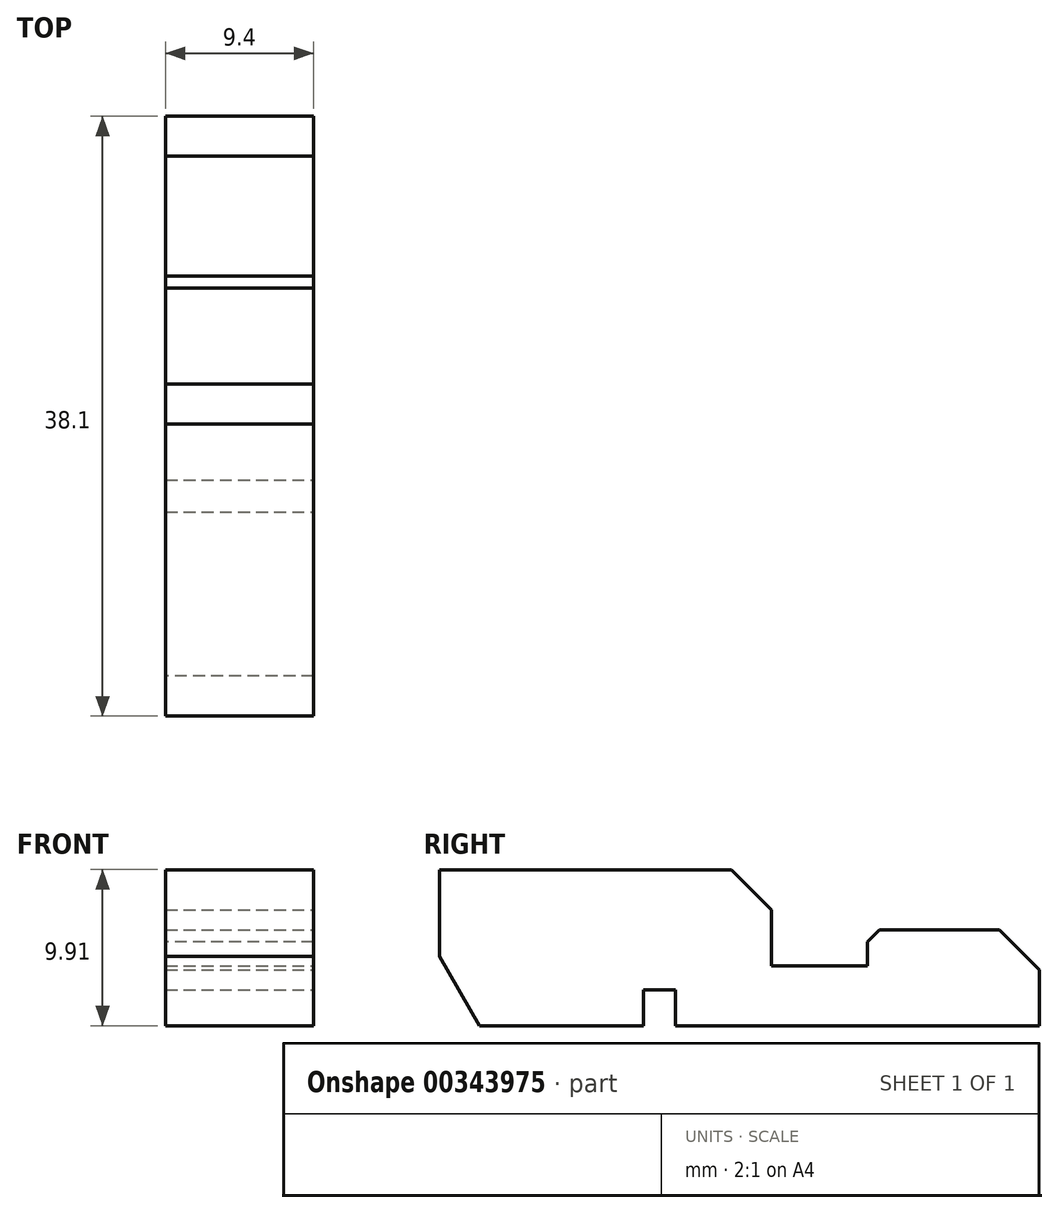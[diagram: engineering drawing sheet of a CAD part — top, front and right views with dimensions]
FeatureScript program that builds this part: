
annotation { "Feature Type Name" : "Feature", "Feature Type Description" : "" }
export const myFeature = defineFeature(function(context is Context, id is Id, definition is map)
    precondition{}
    {
        {
            var Q0;
            Q0=qCreatedBy(makeId("Top.planeOp"),FACE);
            var sketch = newSketch(context, id + "F0", { "sketchPlane" : qUnion([Q0])});
            skLineSegment(sketch, "E0.bottom", {"start": v(4.7, 19.05) * mm, "end": v(-4.7, 19.05) * mm});
            skLineSegment(sketch, "E0.top", {"start": v(4.7, -19.05) * mm, "end": v(-4.7, -19.05) * mm});
            skLineSegment(sketch, "E0.left", {"start": v(4.7, 19.05) * mm, "end": v(4.7, -19.05) * mm});
            skLineSegment(sketch, "E0.right", {"start": v(-4.7, 19.05) * mm, "end": v(-4.7, -19.05) * mm});
            skPoint(sketch, "E0.middle", {"position": v(0, 0) * mm});
            skSolve(sketch);
        }
        {
            var Q0;
            Q0=makeQuery(id+"F0.imprint","IMPRINT",FACE,{"disambiguationData":[TD([[makeQuery(id+"F0.imprint","IMPRINT",EDGE,{"derivedFrom":sQuery(id+"F0.wireOp",EDGE,"E0.bottom")}),1.0]])]});
            extrude(context, id + "F1", {"entities" : qUnion([Q0]), "depth" : 6.1 * mm});
        }
        {
            var Q0;
            Q0=makeQuery(id+"F1.opExtrude","CAP_FACE",FACE,{"disambiguationData":[OSD([sQuery(id+"F0.wireOp",EDGE,"E0.bottom"),sQuery(id+"F0.wireOp",EDGE,"E0.top"),sQuery(id+"F0.wireOp",EDGE,"E0.left"),sQuery(id+"F0.wireOp",EDGE,"E0.right")])],"isStart":false});
            var sketch = newSketch(context, id + "F2", { "sketchPlane" : qUnion([Q0])});
            skPoint(sketch, "E1", {"position": v(-4.7, 5.08) * mm});
            skPoint(sketch, "E2", {"position": v(4.7, 5.08) * mm});
            skPoint(sketch, "E3", {"position": v(0, 5.08) * mm});
            skLineSegment(sketch, "E4.bottom", {"start": v(-4.7, 8.13) * mm, "end": v(4.7, 8.13) * mm});
            skLineSegment(sketch, "E4.top", {"start": v(-4.7, 2.03) * mm, "end": v(4.7, 2.03) * mm});
            skLineSegment(sketch, "E4.left", {"start": v(-4.7, 8.13) * mm, "end": v(-4.7, 2.03) * mm});
            skLineSegment(sketch, "E4.right", {"start": v(4.7, 8.13) * mm, "end": v(4.7, 2.03) * mm});
            skLineSegment(sketch, "E5", {"start": v(-4.7, 5.08) * mm, "end": v(4.7, 5.08) * mm});
            skSolve(sketch);
        }
        {
            var Q0;
            {var subQ0=sQuery(id+"F2.wireOp",EDGE,"E4.bottom");Q0=makeQuery(id+"F2.imprint","IMPRINT",FACE,{"disambiguationData":[TD([[makeQuery(id+"F2.imprint","IMPRINT",EDGE,{"derivedFrom":subQ0}),-1.0]])]});}
            var Q1;
            {var subQ0=sQuery(id+"F2.wireOp",EDGE,"E4.top");Q1=makeQuery(id+"F2.imprint","IMPRINT",FACE,{"disambiguationData":[TD([[makeQuery(id+"F2.imprint","IMPRINT",EDGE,{"derivedFrom":subQ0}),1.0]])]});}
            extrude(context, id + "F3", {"entities" : qUnion([Q0, Q1]), "operationType" : NewBodyOperationType.REMOVE, "oppositeDirection" : true, "depth" : 2.3 * mm});
        }
        {
            var Q0;
            Q0=makeQuery(id+"F1.opExtrude","CAP_FACE",FACE,{"disambiguationData":[OSD([sQuery(id+"F0.wireOp",EDGE,"E0.bottom"),sQuery(id+"F0.wireOp",EDGE,"E0.top"),sQuery(id+"F0.wireOp",EDGE,"E0.left"),sQuery(id+"F0.wireOp",EDGE,"E0.right")])],"isStart":true});
            var sketch = newSketch(context, id + "F4", { "sketchPlane" : qUnion([Q0])});
            skPoint(sketch, "E6", {"position": v(-4.7, 5.08) * mm});
            skPoint(sketch, "E7", {"position": v(4.7, 5.08) * mm});
            skLineSegment(sketch, "E8", {"start": v(-4.7, 5.08) * mm, "end": v(4.7, 5.08) * mm});
            skPoint(sketch, "E9", {"position": v(0, 5.08) * mm});
            skLineSegment(sketch, "E10.bottom", {"start": v(-4.7, 6.1) * mm, "end": v(4.7, 6.1) * mm});
            skLineSegment(sketch, "E10.top", {"start": v(-4.7, 4.06) * mm, "end": v(4.7, 4.06) * mm});
            skLineSegment(sketch, "E10.left", {"start": v(-4.7, 6.1) * mm, "end": v(-4.7, 4.06) * mm});
            skLineSegment(sketch, "E10.right", {"start": v(4.7, 6.1) * mm, "end": v(4.7, 4.06) * mm});
            skSolve(sketch);
        }
        {
            var Q0;
            Q0 = qSketchRegion(id + "F4", true);
            extrude(context, id + "F5", {"entities" : qUnion([Q0]), "operationType" : NewBodyOperationType.REMOVE, "oppositeDirection" : true, "depth" : 2.3 * mm});
        }
        {
            var Q0;
            Q0=makeQuery(id+"F1.opExtrude","CAP_EDGE",EDGE,{"disambiguationData":[OSD([sQuery(id+"F0.wireOp",EDGE,"E0.top")])],"isStart":true});
            chamfer(context, id + "F6", {"entities" : qUnion([Q0]), "chamferType" : ChamferType.OFFSET_ANGLE, "width" : 2.54 * mm, "oppositeDirection" : false, "angle" : 60 * degree, "tangentPropagation" : true});
        }
        {
            var Q0;
            Q0=makeQuery(id+"F1.opExtrude","CAP_EDGE",EDGE,{"disambiguationData":[OSD([sQuery(id+"F0.wireOp",EDGE,"E0.bottom")])],"isStart":false});
            chamfer(context, id + "F7", {"entities" : qUnion([Q0]), "width" : 2.54 * mm, "tangentPropagation" : true});
        }
        {
            var Q0;
            {var subQ0=sQuery(id+"F0.wireOp",EDGE,"E0.top");var subQ1=sQuery(id+"F0.wireOp",EDGE,"E0.left");var subQ2=sQuery(id+"F0.wireOp",EDGE,"E0.right");Q0=makeQuery(id+"F3.boolean.opBoolean","SPLIT",FACE,{"disambiguationData":[TD([makeQuery(id+"F1.opExtrude","SWEPT_FACE",FACE,{"disambiguationData":[OSD([subQ0])]})])],"derivedFrom":makeQuery(id+"F1.opExtrude","CAP_FACE",FACE,{"disambiguationData":[OSD([sQuery(id+"F0.wireOp",EDGE,"E0.bottom"),subQ0,subQ1,subQ2])],"isStart":false})});}
            extrude(context, id + "F8", {"entities" : qUnion([Q0]), "operationType" : NewBodyOperationType.ADD, "depth" : 3.8 * mm});
        }
        {
            var Q0;
            Q0=makeQuery(id+"F8.opExtrude","CAP_EDGE",EDGE,{"disambiguationData":[OSD([sQuery(id+"F2.wireOp",EDGE,"E4.top")])],"isStart":false});
            var Q1;
            Q1=makeQuery(id+"F8.opExtrude","CAP_EDGE",EDGE,{"disambiguationData":[OSD([sQuery(id+"F0.wireOp",EDGE,"E0.bottom"),sQuery(id+"F0.wireOp",EDGE,"E0.top"),sQuery(id+"F0.wireOp",EDGE,"E0.left"),sQuery(id+"F0.wireOp",EDGE,"E0.right")])],"isStart":false});
            chamfer(context, id + "F9", {"entities" : qUnion([Q0, Q1]), "width" : 2.54 * mm, "tangentPropagation" : true});
        }
        {
            var Q0;
            Q0=makeQuery(id+"F3.boolean.opBoolean","COPY",EDGE,{"derivedFrom":makeQuery(id+"F3.opExtrude","CAP_EDGE",EDGE,{"disambiguationData":[OSD([sQuery(id+"F2.wireOp",EDGE,"E4.bottom")])],"isStart":true})});
            chamfer(context, id + "F10", {"entities" : qUnion([Q0]), "width" : 0.76 * mm, "tangentPropagation" : true});
        }
    });
